FCSTD DOCUMENT  (FreeCAD 0.19R19373 (Git))
Label: asm_base_serv0_v019
License: All rights reserved
LicenseURL: http://en.wikipedia.org/wiki/All_rights_reserved
objects: App::DocumentObjectGroup×3, App::Link×3, PartDesign::CoordinateSystem×1, App::FeaturePython×1, App::Part×1
note: 1 computed .brp shape members not serialized (recipe doc carries the construction recipe); baked Part::Feature solids carry a one-line shape summary decoded from their .brp
EXTERNAL_REF file=../Supp_servo/supp_servo_base.FCStd obj=LCS_Origin
EXTERNAL_REF file=../Supp_servo/supp_servo_base.FCStd obj=Model
EXTERNAL_REF file=futuba_s3003.FCStd obj=LCS_Origin
EXTERNAL_REF file=futuba_s3003.FCStd obj=Model

FEATURE [App::DocumentObjectGroup] Parts
FEATURE [PartDesign::CoordinateSystem] LCS_Origin
  AttacherType = Attacher::AttachEngine3D
  MapMode = 2
  Support = -> [X_Axis]
FEATURE [App::DocumentObjectGroup] Constraints
FEATURE [App::FeaturePython] Variables  # WARN: FeaturePython — macro-defined, semantics opaque (R4)
FEATURE [App::DocumentObjectGroup] Group  label="Groupe"
FEATURE [App::Link] supp_servo_base
  AssemblyType = Asm4EE
  AttachedBy = #LCS_Origin
  AttachedTo = Parent Assembly#LCS_Origin
  LinkedObject = -> <external ../Supp_servo/supp_servo_base.FCStd>#Model
  expr: Placement = LCS_Origin.Placement * AttachmentOffset * supp_servo_base#LCS_Origin.Placement ^ -1
FEATURE [App::Link] supp_servo_base001
  AssemblyType = Asm4EE
  AttachedBy = #LCS_Origin
  AttachedTo = Parent Assembly#LCS_Origin
  LinkedObject = -> <external ../Supp_servo/supp_servo_base.FCStd>#Model
  expr: Placement = LCS_Origin.Placement * AttachmentOffset * supp_servo_base#LCS_Origin.Placement ^ -1
FEATURE [App::Link] futuba_s3003
  AssemblyType = Asm4EE
  AttachedBy = #LCS_Origin
  AttachedTo = supp_servo_base#LCS_Origin
  LinkedObject = -> <external futuba_s3003.FCStd>#Model
  expr: Placement = supp_servo_base.Placement * supp_servo_base#LCS_Origin.Placement * AttachmentOffset * futuba_s3003#LCS_Origin.Placement ^ -1
FEATURE [App::Part] Model
  Configuration = 0
  Group = -> [LCS_Origin,Constraints,Variables,supp_servo_base,supp_servo_base001,futuba_s3003]
  Origin = -> Origin
  Type = Assembly4 Model

RESOLVED EXTERNAL PARTS (link-assembly join: the EXTERNAL_REF files above that resolve inside this repo's crawl, each included once):
---- part ../Supp_servo/supp_servo_base.FCStd = doc fcstd_2c1204837815 ----
FCSTD DOCUMENT  (FreeCAD 0.18R16131 (Git))
Label: supp_servo_base
License: All rights reserved
LicenseURL: http://en.wikipedia.org/wiki/All_rights_reserved
objects: Sketcher::SketchObject×9, PartDesign::Pocket×8, App::DocumentObjectGroup×2, PartDesign::Pad×1, PartDesign::Body×1, PartDesign::CoordinateSystem×1, App::FeaturePython×1, App::Part×1
note: 29 computed .brp shape members not serialized (recipe doc carries the construction recipe); baked Part::Feature solids carry a one-line shape summary decoded from their .brp

FEATURE [Sketcher::SketchObject] Sketch
  MapMode = 5
  Support = -> [XY_Plane]
  sketch-geometry (4):
    g0: LineSegment StartX=0 StartY=0 StartZ=0 EndX=25 EndY=0 EndZ=0
    g1: LineSegment StartX=25 StartY=0 StartZ=0 EndX=25 EndY=60 EndZ=0
    g2: LineSegment StartX=25 StartY=60 StartZ=0 EndX=0 EndY=60 EndZ=0
    g3: LineSegment StartX=0 StartY=60 StartZ=0 EndX=0 EndY=0 EndZ=0
  constraints (11):
    c: Coincident(g0,g1)
    c: Coincident(g1,g2)
    c: Coincident(g2,g3)
    c: Coincident(g3,g0)
    c: Horizontal(g0)
    c: Horizontal(g2)
    c: Vertical(g1)
    c: Vertical(g3)
    c: Coincident(g0,g-1)
    c: DistanceY(g3,g3) = 60
    c: DistanceX(g0,g0) = 25
FEATURE [PartDesign::Pad] Pad
  Length = 30
  Length2 = 100
  Profile = -> Sketch
  Type = 0
FEATURE [Sketcher::SketchObject] Sketch001
  ExternalGeometry = -> [Pad]
  MapMode = 5
  Placement = pos=(0,0,30) rot=(0,0,1;0rad)
  Support = -> [Pad]
  sketch-geometry (11):
    g0: GeomPoint X=12.5 Y=60 Z=0
    g1: GeomPoint X=12.5 Y=0 Z=0
    g2: GeomPoint X=12.5 Y=30 Z=0
    g3: GeomPoint X=12.5 Y=50 Z=0
    g4: GeomPoint X=12.5 Y=10 Z=0
    g5: LineSegment StartX=2.5 StartY=10 StartZ=0 EndX=22.5 EndY=10 EndZ=0
    g6: LineSegment StartX=22.5 StartY=10 StartZ=0 EndX=22.5 EndY=50 EndZ=0
    g7: LineSegment StartX=22.5 StartY=50 StartZ=0 EndX=2.5 EndY=50 EndZ=0
    g8: LineSegment StartX=2.5 StartY=50 StartZ=0 EndX=2.5 EndY=10 EndZ=0
    g9: GeomPoint X=12.5 Y=10 Z=0
    g10: GeomPoint X=0 Y=10 Z=0
  constraints (23):
    c: PointOnObject(g0,g-3)
    c: DistanceX(g-3,g0) = 12.5
    c: PointOnObject(g1,g-4)
    c: DistanceX(g1,g-1) = -12.5
    c: DistanceY(g1,g2) = 30
    c: DistanceY(g3,g0) = 10
    c: DistanceY(g1,g4) = 10
    c: Coincident(g5,g6)
    c: Coincident(g6,g7)
    c: Coincident(g7,g8)
    c: Coincident(g8,g5)
    c: Horizontal(g5)
    c: Horizontal(g7)
    c: Vertical(g6)
    c: Vertical(g8)
    c: DistanceX(g5,g5) = 20
    c: DistanceY(g6,g6) = 40
    c: PointOnObject(g9,g5)
    c: DistanceX(g5,g9) = 10
    c: Coincident(g9,g4)
    c: PointOnObject(g10,g-5)
    c: DistanceY(g-1,g10) = 10
    c: DistanceX(g10,g5) = 2.5
FEATURE [PartDesign::Pocket] Pocket
  BaseFeature = -> Pad
  Length = 27
  Length2 = 100
  Profile = -> Sketch001
  Type = 0
FEATURE [Sketcher::SketchObject] Sketch002
  ExternalGeometry = -> [Pocket]
  MapMode = 5
  Placement = pos=(0,0,30) rot=(0,0,1;0rad)
  Support = -> [Pocket]
  sketch-geometry (4):
    g0: LineSegment StartX=0 StartY=45 StartZ=0 EndX=2.5 EndY=45 EndZ=0
    g1: LineSegment StartX=2.5 StartY=45 StartZ=0 EndX=2.5 EndY=15 EndZ=0
    g2: LineSegment StartX=2.5 StartY=15 StartZ=0 EndX=0 EndY=15 EndZ=0
    g3: LineSegment StartX=0 StartY=15 StartZ=0 EndX=0 EndY=45 EndZ=0
  constraints (12):
    c: Coincident(g0,g1)
    c: Coincident(g1,g2)
    c: Coincident(g2,g3)
    c: Coincident(g3,g0)
    c: Horizontal(g0)
    c: Horizontal(g2)
    c: Vertical(g1)
    c: Vertical(g3)
    c: PointOnObject(g0,g-4)
    c: DistanceY(g0,g-4) = 5
    c: DistanceX(g0,g0) = 2.5
    c: DistanceY(g1,g1) = 30
FEATURE [Sketcher::SketchObject] Sketch003
  ExternalGeometry = -> [Pocket]
  MapMode = 5
  Placement = pos=(0,0,30) rot=(0,0,1;0rad)
  Support = -> [Pocket]
  sketch-geometry (4):
    g0: LineSegment StartX=22.5 StartY=45 StartZ=0 EndX=25 EndY=45 EndZ=0
    g1: LineSegment StartX=25 StartY=45 StartZ=0 EndX=25 EndY=15 EndZ=0
    g2: LineSegment StartX=25 StartY=15 StartZ=0 EndX=22.5 EndY=15 EndZ=0
    g3: LineSegment StartX=22.5 StartY=15 StartZ=0 EndX=22.5 EndY=45 EndZ=0
  constraints (12):
    c: Coincident(g0,g1)
    c: Coincident(g1,g2)
    c: Coincident(g2,g3)
    c: Coincident(g3,g0)
    c: Horizontal(g0)
    c: Horizontal(g2)
    c: Vertical(g1)
    c: Vertical(g3)
    c: PointOnObject(g0,g-4)
    c: DistanceY(g1,g1) = 30
    c: DistanceY(g0,g-4) = 5
    c: DistanceX(g0,g0) = 2.5
FEATURE [PartDesign::Pocket] Pocket001
  BaseFeature = -> Pocket
  Length = 25
  Length2 = 100
  Profile = -> Sketch002
  Type = 0
FEATURE [PartDesign::Pocket] Pocket002
  BaseFeature = -> Pocket001
  Length = 25
  Length2 = 100
  Profile = -> Sketch003
  Type = 0
FEATURE [Sketcher::SketchObject] Sketch004
  ExternalGeometry = -> [Pocket002]
  MapMode = 5
  Placement = pos=(0,50,0) rot=(1,0,0;1.5708rad)
  Support = -> [Pocket002]
  sketch-geometry (4):
    g0: LineSegment StartX=2.5 StartY=27 StartZ=0 EndX=22.5 EndY=27 EndZ=0
    g1: LineSegment StartX=22.5 StartY=27 StartZ=0 EndX=22.5 EndY=3 EndZ=0
    g2: LineSegment StartX=22.5 StartY=3 StartZ=0 EndX=2.5 EndY=3 EndZ=0
    g3: LineSegment StartX=2.5 StartY=3 StartZ=0 EndX=2.5 EndY=27 EndZ=0
  constraints (12):
    c: Coincident(g0,g1)
    c: Coincident(g1,g2)
    c: Coincident(g2,g3)
    c: Coincident(g3,g0)
    c: Horizontal(g0)
    c: Horizontal(g2)
    c: Vertical(g1)
    c: Vertical(g3)
    c: DistanceY(g0,g-3) = 3
    c: PointOnObject(g0,g-3)
    c: PointOnObject(g0,g-5)
    c: DistanceY(g1,g1) = 24
FEATURE [Sketcher::SketchObject] Sketch005
  ExternalGeometry = -> [Pocket002]
  MapMode = 5
  Placement = pos=(0,10,0) rot=(0,0.707107,0.707107;3.14159rad)
  Support = -> [Pocket002]
  sketch-geometry (4):
    g0: LineSegment StartX=-22.5 StartY=27 StartZ=0 EndX=-2.5 EndY=27 EndZ=0
    g1: LineSegment StartX=-2.5 StartY=27 StartZ=0 EndX=-2.5 EndY=3 EndZ=0
    g2: LineSegment StartX=-2.5 StartY=3 StartZ=0 EndX=-22.5 EndY=3 EndZ=0
    g3: LineSegment StartX=-22.5 StartY=3 StartZ=0 EndX=-22.5 EndY=27 EndZ=0
  constraints (12):
    c: Coincident(g0,g1)
    c: Coincident(g1,g2)
    c: Coincident(g2,g3)
    c: Coincident(g3,g0)
    c: Horizontal(g0)
    c: Horizontal(g2)
    c: Vertical(g1)
    c: Vertical(g3)
    c: DistanceY(g0,g-3) = 3
    c: PointOnObject(g0,g-4)
    c: PointOnObject(g0,g-5)
    c: DistanceY(g1,g1) = 24
FEATURE [PartDesign::Pocket] Pocket003
  BaseFeature = -> Pocket002
  Length = 7
  Length2 = 100
  Profile = -> Sketch004
  Type = 0
FEATURE [PartDesign::Pocket] Pocket004
  BaseFeature = -> Pocket003
  Length = 7
  Length2 = 100
  Profile = -> Sketch005
  Type = 0
FEATURE [Sketcher::SketchObject] Sketch006
  ExternalGeometry = -> [Pocket004]
  MapMode = 5
  Placement = pos=(0,60,0) rot=(0,0.707107,0.707107;3.14159rad)
  Support = -> [Pocket004]
  sketch-geometry (4):
    g0: LineSegment StartX=-17.5 StartY=10 StartZ=0 EndX=-7.5 EndY=10 EndZ=0
    g1: LineSegment StartX=-7.5 StartY=10 StartZ=0 EndX=-7.5 EndY=3 EndZ=0
    g2: LineSegment StartX=-7.5 StartY=3 StartZ=0 EndX=-17.5 EndY=3 EndZ=0
    g3: LineSegment StartX=-17.5 StartY=3 StartZ=0 EndX=-17.5 EndY=10 EndZ=0
  constraints (12):
    c: Coincident(g0,g1)
    c: Coincident(g1,g2)
    c: Coincident(g2,g3)
    c: Coincident(g3,g0)
    c: Horizontal(g0)
    c: Horizontal(g2)
    c: Vertical(g1)
    c: Vertical(g3)
    c: DistanceY(g-3,g2) = 3
    c: DistanceX(g2,g2) = 10
    c: DistanceY(g1,g1) = 7
    c: DistanceX(g-3,g2) = 7.5
FEATURE [PartDesign::Pocket] Pocket005
  BaseFeature = -> Pocket004
  Length = 5
  Length2 = 100
  Profile = -> Sketch006
  Type = 1
FEATURE [Sketcher::SketchObject] Sketch007
  ExternalGeometry = -> [Pocket005]
  MapMode = 5
  Placement = pos=(0,0,30) rot=(0,0,1;0rad)
  Support = -> [Pocket005]
  sketch-geometry (4):
    g0: GeomPoint X=0 Y=5 Z=0
    g1: GeomPoint X=25 Y=5 Z=0
    g2: Circle CenterX=6 CenterY=5 CenterZ=0 NormalX=0 NormalY=0 NormalZ=1 AngleXU=0 Radius=1
    g3: Circle CenterX=19 CenterY=5 CenterZ=0 NormalX=0 NormalY=0 NormalZ=1 AngleXU=0 Radius=1
  constraints (8):
    c: PointOnObject(g0,g-2)
    c: DistanceY(g-1,g0) = 5
    c: PointOnObject(g1,g-3)
    c: DistanceY(g-3,g1) = 5
    c: Radius(g2) = 1
    c: Radius(g3) = 1
    c: DistanceX(g0,g2) = 6
    c: DistanceX(g3,g1) = 6
FEATURE [Sketcher::SketchObject] Sketch008
  ExternalGeometry = -> [Pocket005]
  MapMode = 5
  Placement = pos=(0,0,30) rot=(0,0,1;0rad)
  Support = -> [Pocket005]
  sketch-geometry (4):
    g0: GeomPoint X=0 Y=55 Z=0
    g1: GeomPoint X=25 Y=55 Z=0
    g2: Circle CenterX=6 CenterY=55 CenterZ=0 NormalX=0 NormalY=0 NormalZ=1 AngleXU=0 Radius=1
    g3: Circle CenterX=19 CenterY=55 CenterZ=0 NormalX=0 NormalY=0 NormalZ=1 AngleXU=0 Radius=1
  constraints (8):
    c: PointOnObject(g0,g-2)
    c: DistanceY(g0,g-3) = 5
    c: PointOnObject(g1,g-4)
    c: DistanceY(g1,g-4) = 5
    c: Radius(g2) = 1
    c: DistanceX(g0,g2) = 6
    c: Radius(g3) = 1
    c: DistanceX(g3,g1) = 6
FEATURE [PartDesign::Pocket] Pocket006
  BaseFeature = -> Pocket005
  Length = 3
  Length2 = 100
  Profile = -> Sketch007
  Type = 0
FEATURE [PartDesign::Pocket] Pocket007
  BaseFeature = -> Pocket006
  Length = 3
  Length2 = 100
  Profile = -> Sketch008
  Type = 0
FEATURE [PartDesign::Body] Body
  Group = -> [Sketch,Pad,Sketch001,Pocket,Sketch002,Sketch003,Pocket001,Pocket002,Sketch004,Sketch005,Pocket003,Pocket004,Sketch006,Pocket005,Sketch007,Sketch008,Pocket006,Pocket007]
  Origin = -> Origin
  Tip = -> Pocket007
FEATURE [App::DocumentObjectGroup] Parts
FEATURE [PartDesign::CoordinateSystem] LCS_Origin
  AttacherType = Attacher::AttachEngine3D
  MapMode = 2
  Support = -> [X_Axis001]
FEATURE [App::DocumentObjectGroup] Constraints
FEATURE [App::FeaturePython] Variables  # WARN: FeaturePython — macro-defined, semantics opaque (R4)
FEATURE [App::Part] Model
  Group = -> [LCS_Origin,Constraints,Variables,Body]
  Origin = -> Origin001
  Type = Assembly4 Model
